# Revit family: Soft Edge 12
name_source: partatom
category: Furniture
revit_build: Autodesk Revit 2016 (Build: 20161004_0715(x64)
units: mm (PartAtom-declared; Revit-internal decimal feet)

## family parameters
Always vertical = Yes
Cut with Voids When Loaded = No
OmniClass Number = 23.40.20.00
OmniClass Title = General Furniture and Specialties
Room Calculation Point = No
Shared = No
Work Plane-Based = No

## types (1)
- Soft Edge 12
    Backrest Shell = HAY Matt laquered Oak Horizontal
    Base = HAY Matt laquered Oak Horizontal
    Depth = 52.5cm - 20.6inch
    Description = Stackable chair with strong curves, extreme lightness and human-centric comfort. Seat and backrest in moulded plywood with wooden frame in different colours. Ideal for many public and private settings – from classrooms and cafés to dining and work areas at home.
    Design = Iskos-Berlin
    Height = 79cm - 20.6inch
    Legs = HAY Matt laquered Oak Vertical
    Manufacturer = HAY
    Model = Soft Edge 12
    Optional gliders = Felt glider, Soft felt glider
    Price = Contact HAY or visit hay.dk
    Seat = HAY Matt laquered Oak Horizontal
    Seat Height = 47.5cm - 18.7inch
    Strength, durability and safety = EN 16139:2013 L2, ANSI/BIFMA X5.4-2012
    Type Comments = Moulded plywood seat and back. Solid oak base.
    URL = https://hay.dk
    Variations = Variability of seat and base colours and finishes. Also available with seat upholstery in selected fabrics and leathers.
    Width = 51.5cm - 20.2inch

## geometry (parser evidence)
native form markers: Sweep x2
no freeform markers — native parametric forms only
